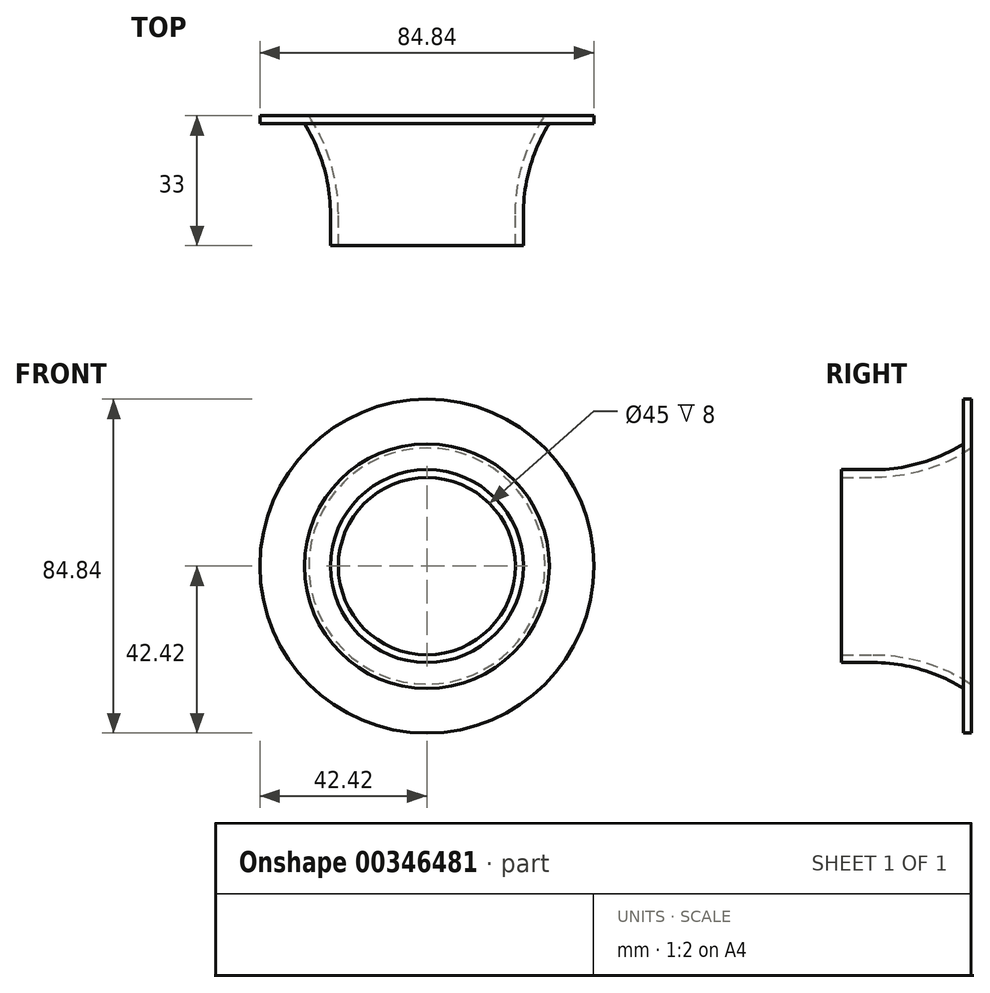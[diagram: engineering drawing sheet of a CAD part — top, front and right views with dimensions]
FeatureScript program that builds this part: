
annotation { "Feature Type Name" : "Feature", "Feature Type Description" : "" }
export const myFeature = defineFeature(function(context is Context, id is Id, definition is map)
    precondition{}
    {
        {
            var Q0;
            Q0=qCreatedBy(makeId("Top.planeOp"),FACE);
            var sketch = newSketch(context, id + "F0", { "sketchPlane" : qUnion([Q0])});
            skPoint(sketch, "E0", {"position": v(22.5, 0) * mm});
            skLineSegment(sketch, "E1", {"start": v(22.5, 0) * mm, "end": v(22.5, 8) * mm});
            skArc(sketch, "E2", {"start": v(30, 33) * mm, "mid": v(24.42, 21.05) * mm, "end": v(22.5, 8) * mm});
            skLineSegment(sketch, "E3", {"start": v(0, 0) * mm, "end": v(0, 72.63) * mm, "construction": true});
            skArc(sketch, "E4.0", {"start": v(31.1, 31) * mm, "mid": v(26.18, 19.96) * mm, "end": v(24.5, 8) * mm});
            skLineSegment(sketch, "E4.1", {"start": v(24.5, 0) * mm, "end": v(24.5, 8) * mm});
            skLineSegment(sketch, "E5", {"start": v(22.5, 0) * mm, "end": v(24.5, 0) * mm});
            skLineSegment(sketch, "E6", {"start": v(32.42, 33) * mm, "end": v(42.42, 33) * mm});
            skLineSegment(sketch, "E7", {"start": v(36.2, 33) * mm, "end": v(36.2, 36.9) * mm, "construction": true});
            skLineSegment(sketch, "E8.MirrorCS", {"start": v(36.2, 88.9) * mm, "end": v(36.2, 85) * mm, "construction": true});
            skLineSegment(sketch, "E9.MirrorCS", {"start": v(36.2, 85) * mm, "end": v(36.2, 88.9) * mm, "construction": true});
            skLineSegment(sketch, "E10", {"start": v(32.42, 33) * mm, "end": v(30, 33) * mm});
            skLineSegment(sketch, "E11", {"start": v(42.42, 33) * mm, "end": v(42.42, 31) * mm});
            skLineSegment(sketch, "E12", {"start": v(42.42, 31) * mm, "end": v(31.1, 31) * mm});
            skPoint(sketch, "E13.start.orphan", {"position": v(36.2, 34.95) * mm});
            skSolve(sketch);
        }
        {
            var Q0;
            Q0=qCreatedBy(makeId("Front.planeOp"),FACE);
            var sketch = newSketch(context, id + "F1", { "sketchPlane" : qUnion([Q0])});
            skCircle(sketch, "E14", {"center": v(0, 0) * mm, "radius": 22.16 * mm});
            skSolve(sketch);
        }
        {
            var Q0;
            Q0=makeQuery(id+"F0.imprint","IMPRINT",FACE,{"disambiguationData":[TD([[makeQuery(id+"F0.imprint","IMPRINT",EDGE,{"derivedFrom":sQuery(id+"F0.wireOp",EDGE,"E1")}),-1.0]])]});
            var Q1;
            Q1=sQuery(id+"F1.wireOp",EDGE,"E14");
            revolve(context, id + "F2", {"entities" : qUnion([Q0]), "axis" : qUnion([Q1]), "revolveType" : RevolveType.FULL});
        }
    });
